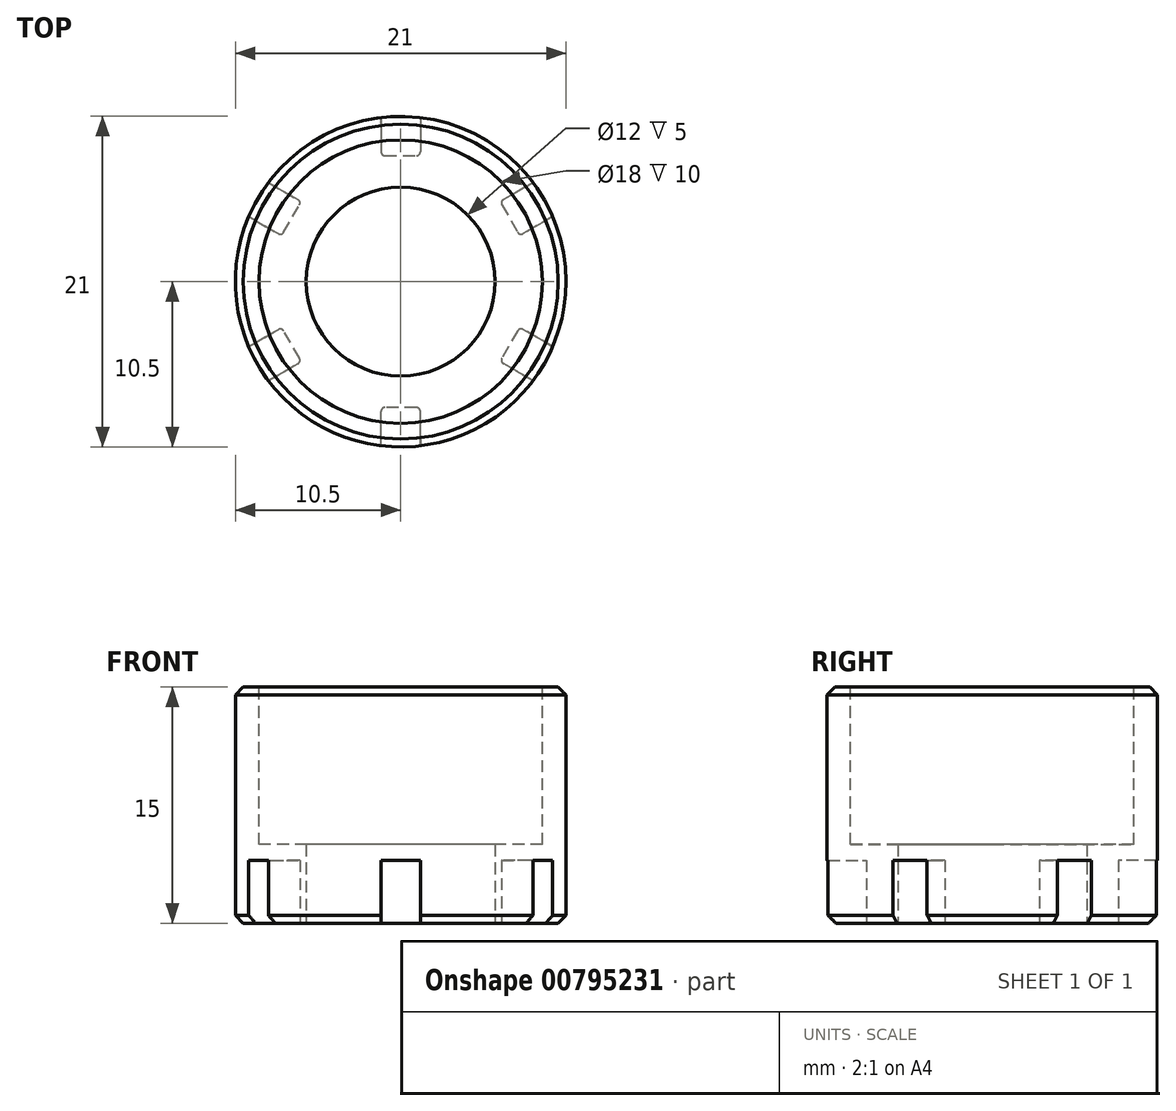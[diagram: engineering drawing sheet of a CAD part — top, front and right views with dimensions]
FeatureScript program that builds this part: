
annotation { "Feature Type Name" : "Feature", "Feature Type Description" : "" }
export const myFeature = defineFeature(function(context is Context, id is Id, definition is map)
    precondition{}
    {
        {
            var Q0;
            Q0=qCreatedBy(makeId("Top.planeOp"),FACE);
            var sketch = newSketch(context, id + "F0", { "sketchPlane" : qUnion([Q0])});
            skCircle(sketch, "E0", {"center": v(0, 0) * mm, "radius": 10.5 * mm});
            skCircle(sketch, "E1", {"center": v(0, 0) * mm, "radius": 6 * mm});
            skSolve(sketch);
        }
        {
            var Q0;
            Q0=makeQuery(id+"F0.imprint","IMPRINT",FACE,{"disambiguationData":[TD([[makeQuery(id+"F0.imprint","IMPRINT",EDGE,{"derivedFrom":sQuery(id+"F0.wireOp",EDGE,"E0")}),1.0]])]});
            extrude(context, id + "F1", {"entities" : qUnion([Q0]), "depth" : 15 * mm, "offsetDistance" : 25 * mm});
        }
        {
            var Q0;
            Q0=makeQuery(id+"F1.opExtrude","CAP_FACE",FACE,{"disambiguationData":[OSD([sQuery(id+"F0.wireOp",EDGE,"E0"),sQuery(id+"F0.wireOp",EDGE,"E1")])],"isStart":false});
            var sketch = newSketch(context, id + "F2", { "sketchPlane" : qUnion([Q0])});
            skCircle(sketch, "E2", {"center": v(0, 0) * mm, "radius": 9 * mm});
            skSolve(sketch);
        }
        {
            var Q0;
            Q0=makeQuery(id+"F2.imprint","IMPRINT",FACE,{"disambiguationData":[TD([[makeQuery(id+"F2.imprint","IMPRINT",EDGE,{"derivedFrom":sQuery(id+"F2.wireOp",EDGE,"E2")}),1.0]])]});
            extrude(context, id + "F3", {"entities" : qUnion([Q0]), "operationType" : NewBodyOperationType.REMOVE, "oppositeDirection" : true, "depth" : 10 * mm, "offsetDistance" : 25 * mm});
        }
        {
            var Q0;
            Q0=makeQuery(id+"F1.opExtrude","CAP_FACE",FACE,{"disambiguationData":[OSD([sQuery(id+"F0.wireOp",EDGE,"E0"),sQuery(id+"F0.wireOp",EDGE,"E1")])],"isStart":true});
            var sketch = newSketch(context, id + "F4", { "sketchPlane" : qUnion([Q0])});
            skLineSegment(sketch, "E3", {"start": v(0, 14.48) * mm, "end": v(0, 7.94) * mm, "construction": true});
            skLineSegment(sketch, "E4.bottom", {"start": v(1.25, 13) * mm, "end": v(-1.25, 13) * mm});
            skLineSegment(sketch, "E4.top", {"start": v(1, 8) * mm, "end": v(-1, 8) * mm});
            skLineSegment(sketch, "E4.left", {"start": v(1.25, 13) * mm, "end": v(1.25, 8.25) * mm});
            skLineSegment(sketch, "E4.right", {"start": v(-1.25, 13) * mm, "end": v(-1.25, 8.25) * mm});
            skPoint(sketch, "E4.middle", {"position": v(0, 10.5) * mm});
            skPoint(sketch, "E5.visualSharp", {"position": v(-1.25, 8) * mm});
            skArc(sketch, "E5.filletArc", {"start": v(-1.25, 8.25) * mm, "mid": v(-1.18, 8.07) * mm, "end": v(-1, 8) * mm});
            skPoint(sketch, "E6.visualSharp", {"position": v(1.25, 8) * mm});
            skArc(sketch, "E6.filletArc", {"start": v(1, 8) * mm, "mid": v(1.18, 8.07) * mm, "end": v(1.25, 8.25) * mm});
            skLineSegment(sketch, "E7.1.0", {"start": v(-10.63, 7.58) * mm, "end": v(-6.52, 5.2) * mm});
            skPoint(sketch, "E7.1.1", {"position": v(-9.1, 5.25) * mm});
            skPoint(sketch, "E7.1.2", {"position": v(-7.55, 2.92) * mm});
            skPoint(sketch, "E7.1.3", {"position": v(-6.3, 5.08) * mm});
            skLineSegment(sketch, "E7.1.4", {"start": v(-12.54, 7.24) * mm, "end": v(-6.88, 3.97) * mm, "construction": true});
            skLineSegment(sketch, "E7.1.5", {"start": v(-10.63, 7.58) * mm, "end": v(-11.88, 5.42) * mm});
            skLineSegment(sketch, "E7.1.6", {"start": v(-11.88, 5.42) * mm, "end": v(-7.77, 3.04) * mm});
            skLineSegment(sketch, "E7.1.7", {"start": v(-6.43, 4.87) * mm, "end": v(-7.43, 3.13) * mm});
            skArc(sketch, "E7.1.8", {"start": v(-7.77, 3.04) * mm, "mid": v(-7.58, 3.02) * mm, "end": v(-7.43, 3.13) * mm});
            skArc(sketch, "E7.1.9", {"start": v(-6.43, 4.87) * mm, "mid": v(-6.4, 5.06) * mm, "end": v(-6.52, 5.2) * mm});
            skLineSegment(sketch, "E7.2.0", {"start": v(-11.88, -5.42) * mm, "end": v(-7.77, -3.04) * mm});
            skPoint(sketch, "E7.2.1", {"position": v(-9.1, -5.25) * mm});
            skPoint(sketch, "E7.2.2", {"position": v(-6.3, -5.08) * mm});
            skPoint(sketch, "E7.2.3", {"position": v(-7.55, -2.92) * mm});
            skLineSegment(sketch, "E7.2.4", {"start": v(-12.54, -7.24) * mm, "end": v(-6.88, -3.97) * mm, "construction": true});
            skLineSegment(sketch, "E7.2.5", {"start": v(-11.88, -5.42) * mm, "end": v(-10.63, -7.58) * mm});
            skLineSegment(sketch, "E7.2.6", {"start": v(-10.63, -7.58) * mm, "end": v(-6.52, -5.2) * mm});
            skLineSegment(sketch, "E7.2.7", {"start": v(-7.43, -3.13) * mm, "end": v(-6.43, -4.87) * mm});
            skArc(sketch, "E7.2.8", {"start": v(-6.52, -5.2) * mm, "mid": v(-6.4, -5.06) * mm, "end": v(-6.43, -4.87) * mm});
            skArc(sketch, "E7.2.9", {"start": v(-7.43, -3.13) * mm, "mid": v(-7.58, -3.02) * mm, "end": v(-7.77, -3.04) * mm});
            skLineSegment(sketch, "E7.3.0", {"start": v(-1.25, -13) * mm, "end": v(-1.25, -8.25) * mm});
            skPoint(sketch, "E7.3.1", {"position": v(0, -10.5) * mm});
            skPoint(sketch, "E7.3.2", {"position": v(1.25, -8) * mm});
            skPoint(sketch, "E7.3.3", {"position": v(-1.25, -8) * mm});
            skLineSegment(sketch, "E7.3.4", {"start": v(0, -14.48) * mm, "end": v(0, -7.94) * mm, "construction": true});
            skLineSegment(sketch, "E7.3.5", {"start": v(-1.25, -13) * mm, "end": v(1.25, -13) * mm});
            skLineSegment(sketch, "E7.3.6", {"start": v(1.25, -13) * mm, "end": v(1.25, -8.25) * mm});
            skLineSegment(sketch, "E7.3.7", {"start": v(-1, -8) * mm, "end": v(1, -8) * mm});
            skArc(sketch, "E7.3.8", {"start": v(1.25, -8.25) * mm, "mid": v(1.18, -8.07) * mm, "end": v(1, -8) * mm});
            skArc(sketch, "E7.3.9", {"start": v(-1, -8) * mm, "mid": v(-1.18, -8.07) * mm, "end": v(-1.25, -8.25) * mm});
            skLineSegment(sketch, "E7.4.0", {"start": v(10.63, -7.58) * mm, "end": v(6.52, -5.2) * mm});
            skPoint(sketch, "E7.4.1", {"position": v(9.1, -5.25) * mm});
            skPoint(sketch, "E7.4.2", {"position": v(7.55, -2.92) * mm});
            skPoint(sketch, "E7.4.3", {"position": v(6.3, -5.08) * mm});
            skLineSegment(sketch, "E7.4.4", {"start": v(12.54, -7.24) * mm, "end": v(6.88, -3.97) * mm, "construction": true});
            skLineSegment(sketch, "E7.4.5", {"start": v(10.63, -7.58) * mm, "end": v(11.88, -5.42) * mm});
            skLineSegment(sketch, "E7.4.6", {"start": v(11.88, -5.42) * mm, "end": v(7.77, -3.04) * mm});
            skLineSegment(sketch, "E7.4.7", {"start": v(6.43, -4.87) * mm, "end": v(7.43, -3.13) * mm});
            skArc(sketch, "E7.4.8", {"start": v(7.77, -3.04) * mm, "mid": v(7.58, -3.02) * mm, "end": v(7.43, -3.13) * mm});
            skArc(sketch, "E7.4.9", {"start": v(6.43, -4.87) * mm, "mid": v(6.4, -5.06) * mm, "end": v(6.52, -5.2) * mm});
            skLineSegment(sketch, "E7.5.0", {"start": v(11.88, 5.42) * mm, "end": v(7.77, 3.04) * mm});
            skPoint(sketch, "E7.5.1", {"position": v(9.1, 5.25) * mm});
            skPoint(sketch, "E7.5.2", {"position": v(6.3, 5.08) * mm});
            skPoint(sketch, "E7.5.3", {"position": v(7.55, 2.92) * mm});
            skLineSegment(sketch, "E7.5.4", {"start": v(12.54, 7.24) * mm, "end": v(6.88, 3.97) * mm, "construction": true});
            skLineSegment(sketch, "E7.5.5", {"start": v(11.88, 5.42) * mm, "end": v(10.63, 7.58) * mm});
            skLineSegment(sketch, "E7.5.6", {"start": v(10.63, 7.58) * mm, "end": v(6.52, 5.2) * mm});
            skLineSegment(sketch, "E7.5.7", {"start": v(7.43, 3.13) * mm, "end": v(6.43, 4.87) * mm});
            skArc(sketch, "E7.5.8", {"start": v(6.52, 5.2) * mm, "mid": v(6.4, 5.06) * mm, "end": v(6.43, 4.87) * mm});
            skArc(sketch, "E7.5.9", {"start": v(7.43, 3.13) * mm, "mid": v(7.58, 3.02) * mm, "end": v(7.77, 3.04) * mm});
            skPoint(sketch, "E7.center", {"position": v(0, 0) * mm});
            skSolve(sketch);
        }
        {
            var Q0;
            Q0 = qSketchRegion(id + "F4", true);
            extrude(context, id + "F5", {"entities" : qUnion([Q0]), "operationType" : NewBodyOperationType.REMOVE, "oppositeDirection" : true, "depth" : 4 * mm, "offsetDistance" : 25 * mm});
        }
        {
            var Q0;
            {var subQ0=sQuery(id+"F0.wireOp",EDGE,"E0");Q0=makeQuery(id+"F5.boolean.opBoolean","SPLIT",EDGE,{"disambiguationData":[TD([makeQuery(id+"F5.opExtrude","SWEPT_FACE",FACE,{"disambiguationData":[OSD([sQuery(id+"F4.wireOp",EDGE,"E4.right")])]})])],"derivedFrom":makeQuery(id+"F1.opExtrude","CAP_EDGE",EDGE,{"disambiguationData":[OSD([subQ0])],"isStart":true})});}
            var Q1;
            {var subQ0=sQuery(id+"F0.wireOp",EDGE,"E0");Q1=makeQuery(id+"F5.boolean.opBoolean","SPLIT",EDGE,{"disambiguationData":[TD([makeQuery(id+"F5.opExtrude","SWEPT_FACE",FACE,{"disambiguationData":[OSD([sQuery(id+"F4.wireOp",EDGE,"E4.left")])]})])],"derivedFrom":makeQuery(id+"F1.opExtrude","CAP_EDGE",EDGE,{"disambiguationData":[OSD([subQ0])],"isStart":true})});}
            var Q2;
            {var subQ0=sQuery(id+"F0.wireOp",EDGE,"E0");Q2=makeQuery(id+"F5.boolean.opBoolean","SPLIT",EDGE,{"disambiguationData":[TD([makeQuery(id+"F5.opExtrude","SWEPT_FACE",FACE,{"disambiguationData":[OSD([sQuery(id+"F4.wireOp",EDGE,"E7.4.6")])]})])],"derivedFrom":makeQuery(id+"F1.opExtrude","CAP_EDGE",EDGE,{"disambiguationData":[OSD([subQ0])],"isStart":true})});}
            var Q3;
            {var subQ0=sQuery(id+"F0.wireOp",EDGE,"E0");Q3=makeQuery(id+"F5.boolean.opBoolean","SPLIT",EDGE,{"disambiguationData":[TD([makeQuery(id+"F5.opExtrude","SWEPT_FACE",FACE,{"disambiguationData":[OSD([sQuery(id+"F4.wireOp",EDGE,"E7.3.6")])]})])],"derivedFrom":makeQuery(id+"F1.opExtrude","CAP_EDGE",EDGE,{"disambiguationData":[OSD([subQ0])],"isStart":true})});}
            var Q4;
            {var subQ0=sQuery(id+"F0.wireOp",EDGE,"E0");Q4=makeQuery(id+"F5.boolean.opBoolean","SPLIT",EDGE,{"disambiguationData":[TD([makeQuery(id+"F5.opExtrude","SWEPT_FACE",FACE,{"disambiguationData":[OSD([sQuery(id+"F4.wireOp",EDGE,"E7.2.6")])]})])],"derivedFrom":makeQuery(id+"F1.opExtrude","CAP_EDGE",EDGE,{"disambiguationData":[OSD([subQ0])],"isStart":true})});}
            var Q5;
            {var subQ0=sQuery(id+"F0.wireOp",EDGE,"E0");Q5=makeQuery(id+"F5.boolean.opBoolean","SPLIT",EDGE,{"disambiguationData":[TD([makeQuery(id+"F5.opExtrude","SWEPT_FACE",FACE,{"disambiguationData":[OSD([sQuery(id+"F4.wireOp",EDGE,"E7.1.6")])]})])],"derivedFrom":makeQuery(id+"F1.opExtrude","CAP_EDGE",EDGE,{"disambiguationData":[OSD([subQ0])],"isStart":true})});}
            chamfer(context, id + "F6", {"entities" : qUnion([Q0, Q1, Q2, Q3, Q4, Q5]), "width" : .5 * mm, "tangentPropagation" : true});
        }
        {
            var Q0;
            Q0=makeQuery(id+"F1.opExtrude","CAP_EDGE",EDGE,{"disambiguationData":[OSD([sQuery(id+"F0.wireOp",EDGE,"E0")])],"isStart":false});
            chamfer(context, id + "F7", {"entities" : qUnion([Q0]), "width" : .5 * mm, "tangentPropagation" : true});
        }
    });
